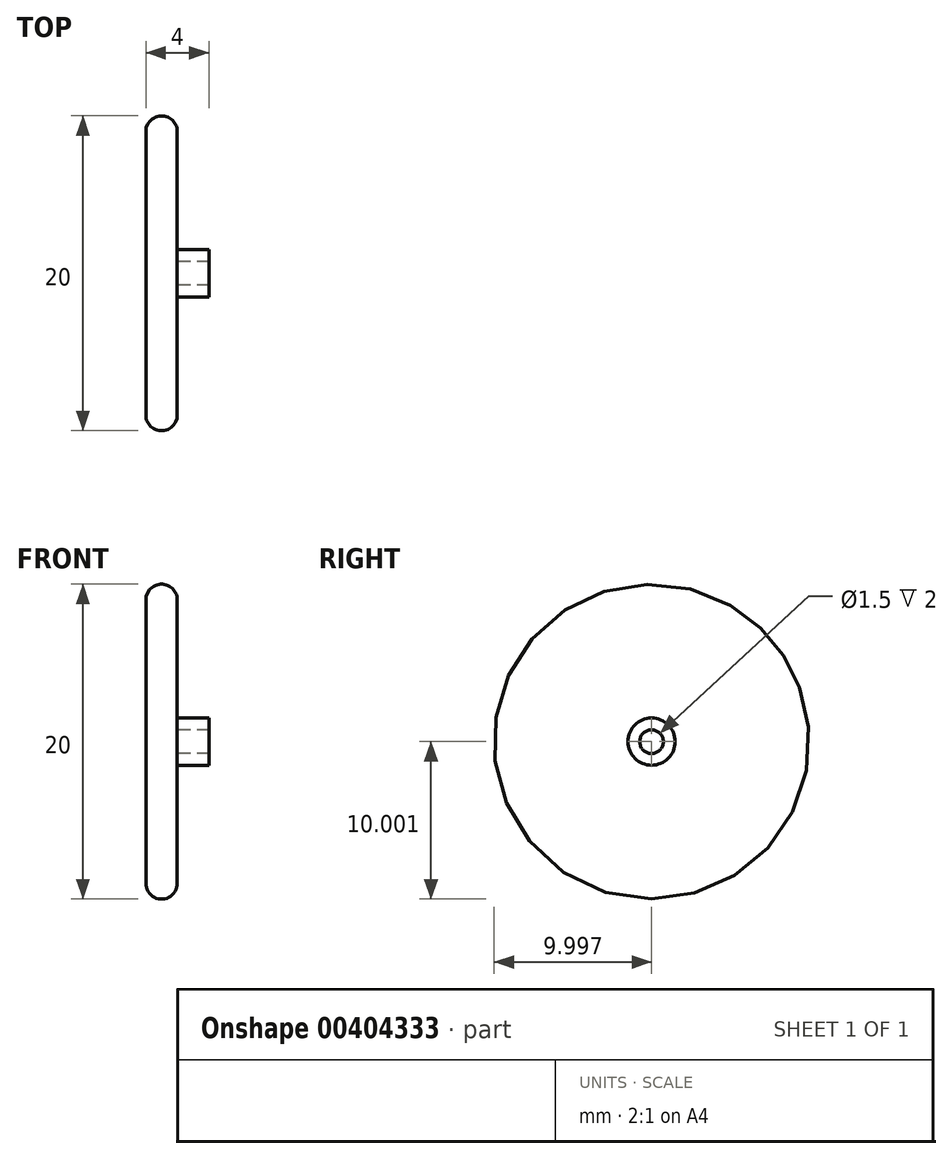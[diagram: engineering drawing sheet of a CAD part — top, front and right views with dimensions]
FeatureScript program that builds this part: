
annotation { "Feature Type Name" : "Feature", "Feature Type Description" : "" }
export const myFeature = defineFeature(function(context is Context, id is Id, definition is map)
    precondition{}
    {
        {
            var Q0;
            Q0=qCreatedBy(makeId("Right.planeOp"),FACE);
            var sketch = newSketch(context, id + "F0", { "sketchPlane" : qUnion([Q0])});
            skCircle(sketch, "E0", {"center": v(36.1, 19.32) * mm, "radius": 10 * mm});
            skSolve(sketch);
        }
        {
            var Q0;
            Q0 = qSketchRegion(id + "F0", true);
            extrude(context, id + "F1", {"entities" : qUnion([Q0]), "depth" : 2 * mm});
        }
        {
            var Q0;
            Q0=makeQuery(id+"F1.opExtrude","CAP_FACE",FACE,{"disambiguationData":[OSD([sQuery(id+"F0.wireOp",EDGE,"E0")])],"isStart":false});
            var sketch = newSketch(context, id + "F2", { "sketchPlane" : qUnion([Q0])});
            skCircle(sketch, "E1", {"center": v(36.1, 19.32) * mm, "radius": 1.5 * mm});
            skCircle(sketch, "E2", {"center": v(36.1, 19.32) * mm, "radius": 0.75 * mm});
            skSolve(sketch);
        }
        {
            var Q0;
            Q0 = qSketchRegion(id + "F2", true);
            extrude(context, id + "F3", {"entities" : qUnion([Q0]), "operationType" : NewBodyOperationType.ADD, "depth" : 2 * mm});
        }
        {
            var Q0;
            Q0=makeQuery(id+"F1.opExtrude","CAP_EDGE",EDGE,{"disambiguationData":[OSD([sQuery(id+"F0.wireOp",EDGE,"E0")])],"isStart":false});
            var Q1;
            Q1=makeQuery(id+"F1.opExtrude","CAP_EDGE",EDGE,{"disambiguationData":[OSD([sQuery(id+"F0.wireOp",EDGE,"E0")])],"isStart":true});
            fillet(context, id + "F4", {"entities" : qUnion([Q0, Q1]), "radius" : 1 * mm, "tangentPropagation" : true, "allowEdgeOverflow" : false});
        }
    });
